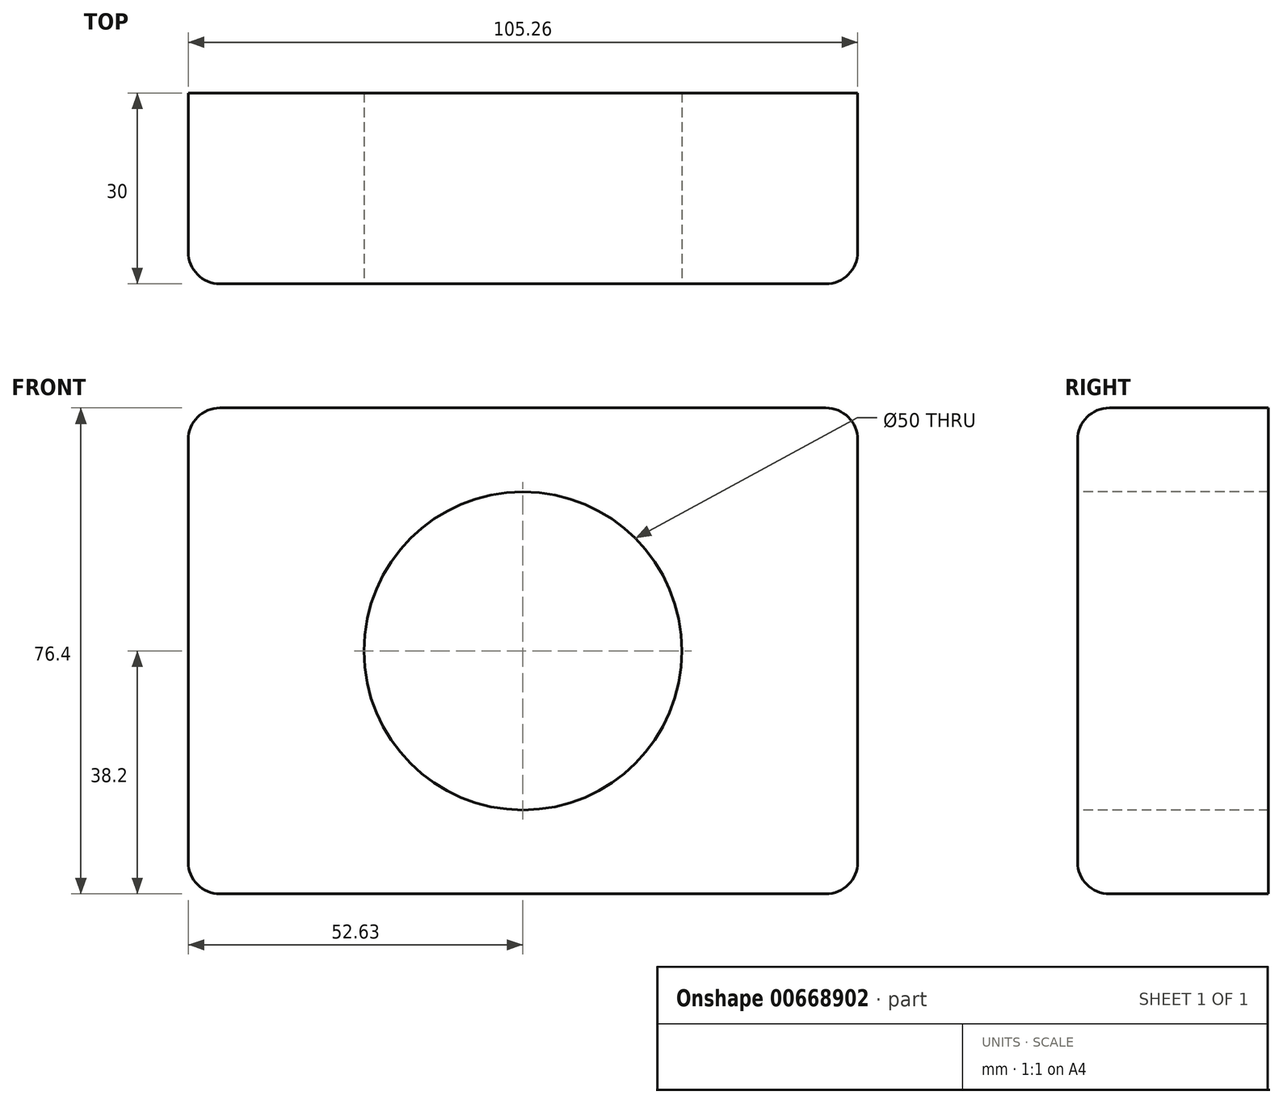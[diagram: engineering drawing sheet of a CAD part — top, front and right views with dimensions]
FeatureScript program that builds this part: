
annotation { "Feature Type Name" : "Feature", "Feature Type Description" : "" }
export const myFeature = defineFeature(function(context is Context, id is Id, definition is map)
    precondition{}
    {
        {
            var Q0;
            Q0=qCreatedBy(makeId("Front.planeOp"),FACE);
            var sketch = newSketch(context, id + "F0", { "sketchPlane" : qUnion([Q0])});
            skLineSegment(sketch, "E0.bottom", {"start": v(52.63, 38.2) * mm, "end": v(-52.63, 38.2) * mm});
            skLineSegment(sketch, "E0.top", {"start": v(52.63, -38.2) * mm, "end": v(-52.63, -38.2) * mm});
            skLineSegment(sketch, "E0.left", {"start": v(52.63, 38.2) * mm, "end": v(52.63, -38.2) * mm});
            skLineSegment(sketch, "E0.right", {"start": v(-52.63, 38.2) * mm, "end": v(-52.63, -38.2) * mm});
            skPoint(sketch, "E0.middle", {"position": v(0, 0) * mm});
            skSolve(sketch);
        }
        {
            var Q0;
            Q0=makeQuery(id+"F0.imprint","IMPRINT",FACE,{"disambiguationData":[TD([[makeQuery(id+"F0.imprint","IMPRINT",EDGE,{"derivedFrom":sQuery(id+"F0.wireOp",EDGE,"E0.bottom")}),1.0]])]});
            extrude(context, id + "F1", {"entities" : qUnion([Q0]), "depth" : 30 * mm, "offsetDistance" : 25 * mm});
        }
        {
            var Q0;
            Q0=makeQuery(id+"F1.opExtrude","CAP_EDGE",EDGE,{"disambiguationData":[OSD([sQuery(id+"F0.wireOp",EDGE,"E0.bottom")])],"isStart":false});
            var Q1;
            Q1=makeQuery(id+"F1.opExtrude","CAP_EDGE",EDGE,{"disambiguationData":[OSD([sQuery(id+"F0.wireOp",EDGE,"E0.right")])],"isStart":false});
            var Q2;
            Q2=makeQuery(id+"F1.opExtrude","CAP_EDGE",EDGE,{"disambiguationData":[OSD([sQuery(id+"F0.wireOp",EDGE,"E0.top")])],"isStart":false});
            var Q3;
            Q3=makeQuery(id+"F1.opExtrude","CAP_EDGE",EDGE,{"disambiguationData":[OSD([sQuery(id+"F0.wireOp",EDGE,"E0.left")])],"isStart":false});
            var Q4;
            Q4=makeQuery(id+"F1.opExtrude","SWEPT_EDGE",EDGE,{"disambiguationData":[OSD([sQuery(id+"F0.wireOp",EDGE,"E0.bottom"),sQuery(id+"F0.wireOp",EDGE,"E0.right")])]});
            var Q5;
            Q5=makeQuery(id+"F1.opExtrude","SWEPT_EDGE",EDGE,{"disambiguationData":[OSD([sQuery(id+"F0.wireOp",EDGE,"E0.top"),sQuery(id+"F0.wireOp",EDGE,"E0.right")])]});
            var Q6;
            Q6=makeQuery(id+"F1.opExtrude","SWEPT_EDGE",EDGE,{"disambiguationData":[OSD([sQuery(id+"F0.wireOp",EDGE,"E0.bottom"),sQuery(id+"F0.wireOp",EDGE,"E0.left")])]});
            var Q7;
            Q7=makeQuery(id+"F1.opExtrude","SWEPT_EDGE",EDGE,{"disambiguationData":[OSD([sQuery(id+"F0.wireOp",EDGE,"E0.top"),sQuery(id+"F0.wireOp",EDGE,"E0.left")])]});
            fillet(context, id + "F2", {"entities" : qUnion([Q0, Q1, Q2, Q3, Q4, Q5, Q6, Q7]), "radius" : 5 * mm, "tangentPropagation" : true, "allowEdgeOverflow" : false});
        }
        {
            var Q0;
            Q0=makeQuery(id+"F1.opExtrude","CAP_FACE",FACE,{"disambiguationData":[OSD([sQuery(id+"F0.wireOp",EDGE,"E0.bottom"),sQuery(id+"F0.wireOp",EDGE,"E0.top"),sQuery(id+"F0.wireOp",EDGE,"E0.left"),sQuery(id+"F0.wireOp",EDGE,"E0.right")])],"isStart":false});
            var sketch = newSketch(context, id + "F3", { "sketchPlane" : qUnion([Q0])});
            skCircle(sketch, "E1", {"center": v(0, 0) * mm, "radius": 25.76 * mm});
            skSolve(sketch);
        }
        {
            var Q0;
            Q0=sQuery(id+"F3.wireOp",VERTEX,"E1.center");
            var Q1;
            Q1=makeQuery(id+"F1.opExtrude","SWEPT_BODY",BODY,{"disambiguationData":[OSD([sQuery(id+"F0.wireOp",EDGE,"E0.bottom"),sQuery(id+"F0.wireOp",EDGE,"E0.top"),sQuery(id+"F0.wireOp",EDGE,"E0.left"),sQuery(id+"F0.wireOp",EDGE,"E0.right")])]});
            hole(context, id + "F4", {"style" : HoleStyle.SIMPLE, "endStyle" : HoleEndStyle.THROUGH, "holeDiameter" : 50 * mm, "majorDiameter" : 5 * mm, "isTappedThrough" : true, "tappedDepth" : 12 * mm, "tapClearance" : 3, "locations" : qUnion([Q0]), "scope" : qUnion([Q1])});
        }
    });
